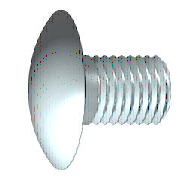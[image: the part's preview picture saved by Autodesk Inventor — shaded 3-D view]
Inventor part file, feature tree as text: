
AUTODESK INVENTOR PART (.ipt)
format: ipt  version: 2020 (Build 240168000, 168)  size: 157,696 bytes
history: native  units: mm (DEFAULTED — no unit token found)
features: plane x1, sketch x1
ambient origin geometry x7: Origin, YZ Plane, XZ Plane, X Axis, Y Axis, Z Axis, Center Point
bodies: Solid1 (feature_tree), Body (feature_tree)
feature tree (2):
  plane  "Work Plane1"
  sketch  "Sketch1"  dims[d0=25.4mm d1=3.683mm d2=6.35mm d3=15.0876mm d4=9.80694mm d8=90.0deg d5=19.05mm d6=0.0mm d7=0.7874mm d10=0.0mm d16=0.0mm d17=0.0mm]
